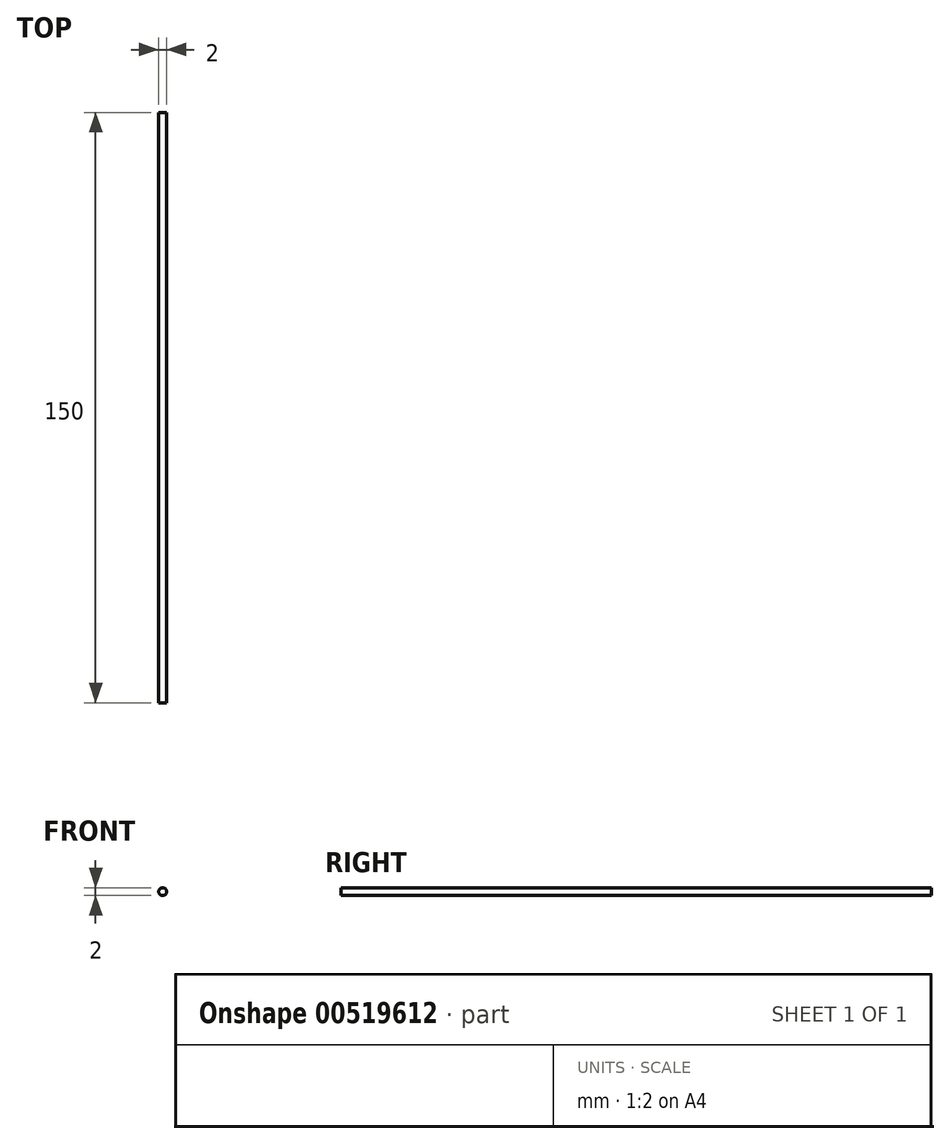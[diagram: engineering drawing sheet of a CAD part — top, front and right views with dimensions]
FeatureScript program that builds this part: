
annotation { "Feature Type Name" : "Feature", "Feature Type Description" : "" }
export const myFeature = defineFeature(function(context is Context, id is Id, definition is map)
    precondition{}
    {
        {
            var Q0;
            Q0=qCreatedBy(makeId("Front.planeOp"),FACE);
            var sketch = newSketch(context, id + "F0", { "sketchPlane" : qUnion([Q0])});
            skCircle(sketch, "E0", {"center": v(0, 0) * mm, "radius": 1 * mm});
            skSolve(sketch);
        }
        {
            var Q0;
            Q0 = qSketchRegion(id + "F0", true);
            extrude(context, id + "F1", {"entities" : qUnion([Q0]), "depth" : 150 * mm, "offsetDistance" : 25 * mm});
        }
    });
